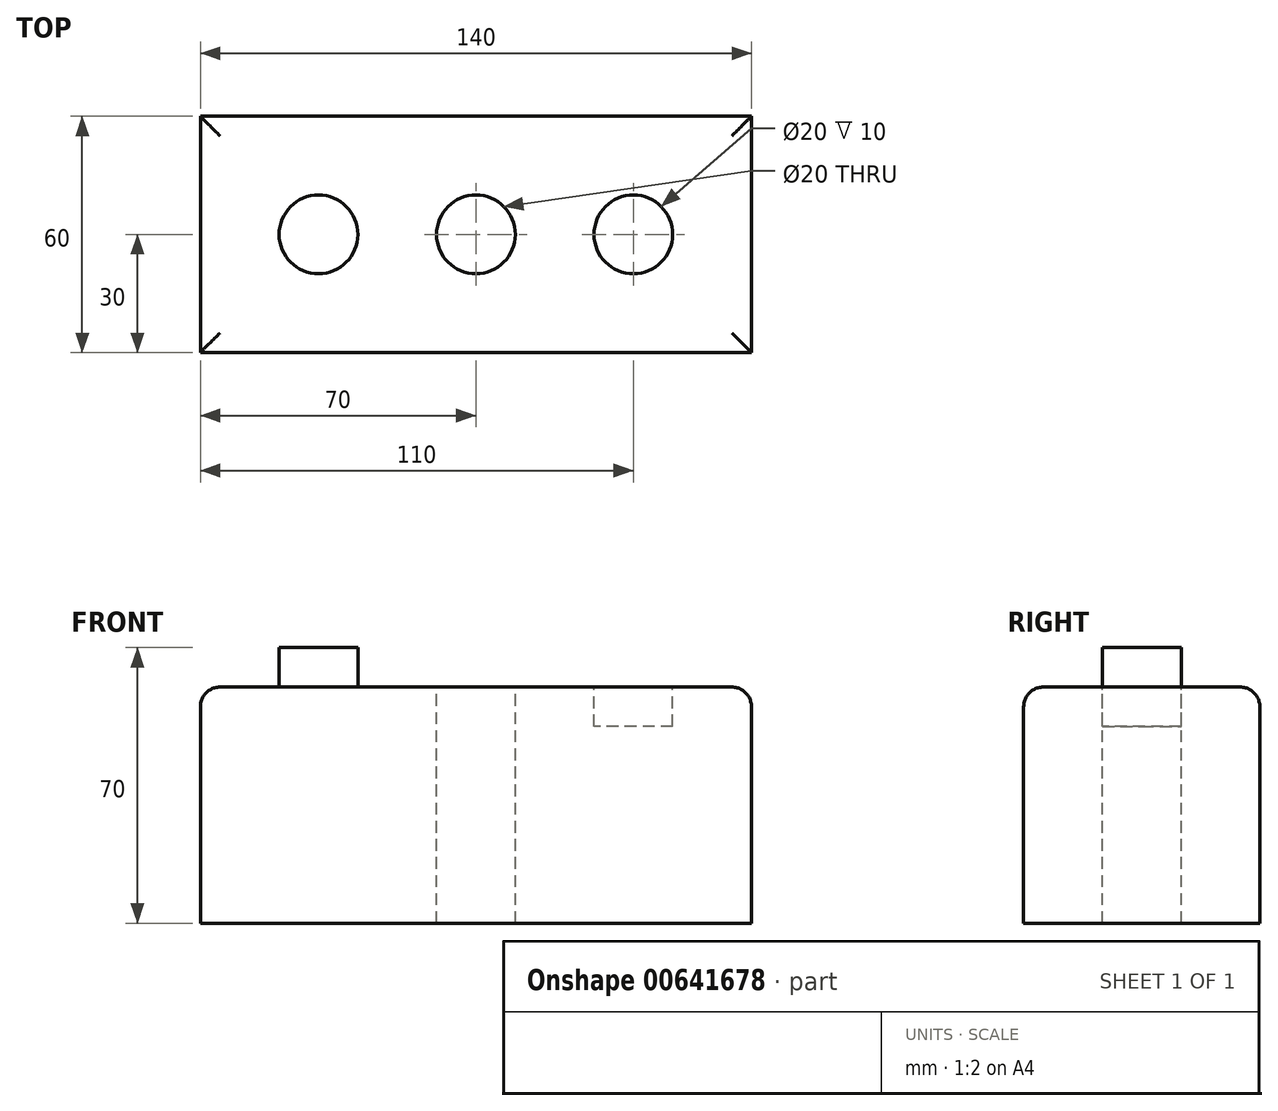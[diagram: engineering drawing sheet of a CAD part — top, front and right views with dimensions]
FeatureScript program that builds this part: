
annotation { "Feature Type Name" : "Feature", "Feature Type Description" : "" }
export const myFeature = defineFeature(function(context is Context, id is Id, definition is map)
    precondition{}
    {
        {
            var Q0;
            Q0=qCreatedBy(makeId("Top.planeOp"),FACE);
            var sketch = newSketch(context, id + "F0", { "sketchPlane" : qUnion([Q0])});
            skLineSegment(sketch, "E0.bottom", {"start": v(70, -30) * mm, "end": v(-70, -30) * mm});
            skLineSegment(sketch, "E0.top", {"start": v(70, 30) * mm, "end": v(-70, 30) * mm});
            skLineSegment(sketch, "E0.left", {"start": v(70, -30) * mm, "end": v(70, 30) * mm});
            skLineSegment(sketch, "E0.right", {"start": v(-70, -30) * mm, "end": v(-70, 30) * mm});
            skPoint(sketch, "E0.middle", {"position": v(0, 0) * mm});
            skSolve(sketch);
        }
        {
            var Q0;
            Q0 = qSketchRegion(id + "F0", true);
            extrude(context, id + "F1", {"entities" : qUnion([Q0]), "depth" : 60 * mm, "offsetDistance" : 25 * mm});
        }
        {
            var Q0;
            Q0=makeQuery(id+"F1.opExtrude","CAP_FACE",FACE,{"disambiguationData":[OSD([sQuery(id+"F0.wireOp",EDGE,"E0.bottom"),sQuery(id+"F0.wireOp",EDGE,"E0.top"),sQuery(id+"F0.wireOp",EDGE,"E0.left"),sQuery(id+"F0.wireOp",EDGE,"E0.right")])],"isStart":false});
            var sketch = newSketch(context, id + "F2", { "sketchPlane" : qUnion([Q0])});
            skCircle(sketch, "E1", {"center": v(-40, 0) * mm, "radius": 10 * mm});
            skSolve(sketch);
        }
        {
            var Q0;
            Q0=makeQuery(id+"F2.imprint","IMPRINT",FACE,{"disambiguationData":[TD([[makeQuery(id+"F2.imprint","IMPRINT",EDGE,{"derivedFrom":sQuery(id+"F2.wireOp",EDGE,"E1")}),-1.0]])]});
            var sketch = newSketch(context, id + "F3", { "sketchPlane" : qUnion([Q0])});
            skCircle(sketch, "E2", {"center": v(40, 0) * mm, "radius": 10 * mm});
            skSolve(sketch);
        }
        {
            var Q0;
            Q0=makeQuery(id+"F2.imprint","IMPRINT",FACE,{"disambiguationData":[TD([[makeQuery(id+"F2.imprint","IMPRINT",EDGE,{"derivedFrom":sQuery(id+"F2.wireOp",EDGE,"E1")}),-1.0]])]});
            var sketch = newSketch(context, id + "F4", { "sketchPlane" : qUnion([Q0])});
            skCircle(sketch, "E3", {"center": v(0, 0) * mm, "radius": 10 * mm});
            skSolve(sketch);
        }
        {
            var Q0;
            Q0 = qSketchRegion(id + "F2", true);
            extrude(context, id + "F5", {"entities" : qUnion([Q0]), "operationType" : NewBodyOperationType.ADD, "depth" : 10 * mm, "offsetDistance" : 25 * mm});
        }
        {
            var Q0;
            Q0 = qSketchRegion(id + "F3", true);
            extrude(context, id + "F6", {"entities" : qUnion([Q0]), "operationType" : NewBodyOperationType.REMOVE, "oppositeDirection" : true, "depth" : 10 * mm, "offsetDistance" : 25 * mm});
        }
        {
            var Q0;
            Q0 = qSketchRegion(id + "F4", true);
            extrude(context, id + "F7", {"entities" : qUnion([Q0]), "operationType" : NewBodyOperationType.REMOVE, "oppositeDirection" : true, "depth" : 109.5 * mm, "offsetDistance" : 25 * mm});
        }
        {
            var Q0;
            Q0=makeQuery(id+"F1.opExtrude","CAP_EDGE",EDGE,{"disambiguationData":[OSD([sQuery(id+"F0.wireOp",EDGE,"E0.right")])],"isStart":false});
            var Q1;
            Q1=makeQuery(id+"F1.opExtrude","CAP_EDGE",EDGE,{"disambiguationData":[OSD([sQuery(id+"F0.wireOp",EDGE,"E0.top")])],"isStart":false});
            var Q2;
            Q2=makeQuery(id+"F1.opExtrude","CAP_EDGE",EDGE,{"disambiguationData":[OSD([sQuery(id+"F0.wireOp",EDGE,"E0.left")])],"isStart":false});
            var Q3;
            Q3=makeQuery(id+"F1.opExtrude","CAP_EDGE",EDGE,{"disambiguationData":[OSD([sQuery(id+"F0.wireOp",EDGE,"E0.bottom")])],"isStart":false});
            fillet(context, id + "F8", {"entities" : qUnion([Q0, Q1, Q2, Q3]), "radius" : 5 * mm, "tangentPropagation" : true, "allowEdgeOverflow" : false});
        }
    });
